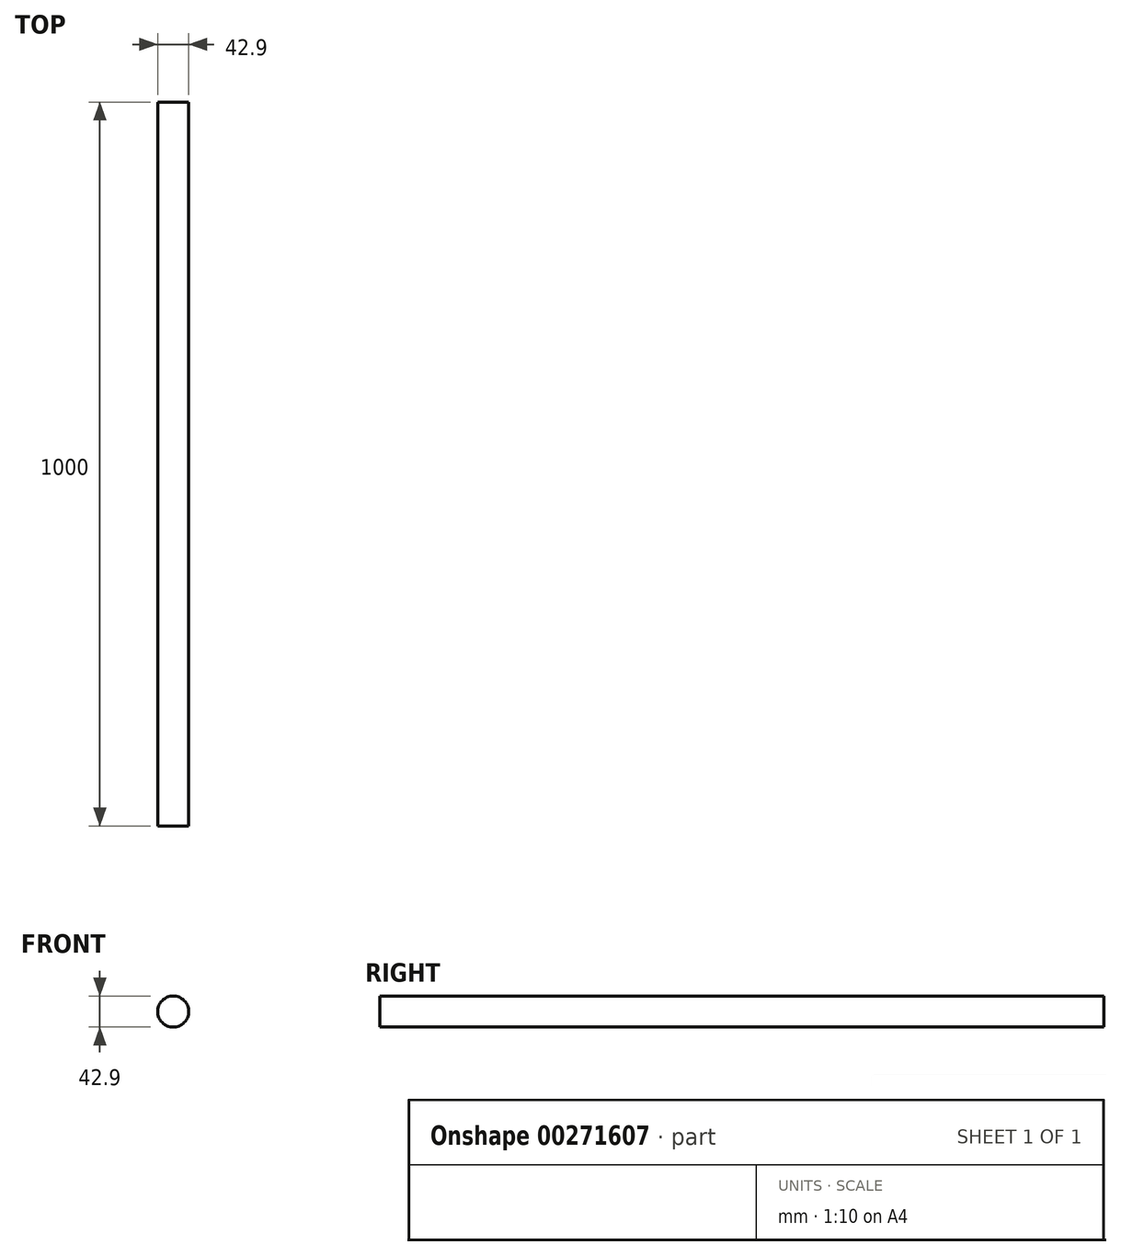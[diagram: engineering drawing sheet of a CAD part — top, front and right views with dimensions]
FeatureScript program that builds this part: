
annotation { "Feature Type Name" : "Feature", "Feature Type Description" : "" }
export const myFeature = defineFeature(function(context is Context, id is Id, definition is map)
    precondition{}
    {
        {
            var Q0;
            Q0=qCreatedBy(makeId("Front.planeOp"),FACE);
            var sketch = newSketch(context, id + "F0", { "sketchPlane" : qUnion([Q0])});
            skCircle(sketch, "E0", {"center": v(0, 0) * mm, "radius": 21.45 * mm});
            skSolve(sketch);
        }
        {
            var Q0;
            Q0 = qSketchRegion(id + "F0", true);
            extrude(context, id + "F1", {"entities" : qUnion([Q0]), "depth" : 1000 * mm});
        }
    });
